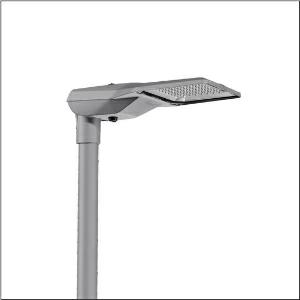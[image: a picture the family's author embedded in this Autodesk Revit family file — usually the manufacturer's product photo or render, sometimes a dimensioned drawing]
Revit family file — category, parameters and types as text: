
# Revit family: streetlight_sl_21_iq_midi___st1_0ab_5xe3m31y08nb_fb51
name_source: partatom
category: Lighting Fixtures
units: mm (PartAtom-declared; Revit-internal decimal feet)

## family parameters
Cut with Voids When Loaded = No
Host = Face
Light Source = No
Part Type = Normal
Room Calculation Point = No
Round Connector Dimension = Use Diameter
Shared = No

## types (1)
- --- (1 x LED, 18970 lm, 136.6 W, 3000K)
    Apparent Load = 137 VA
    CIE Flux Codes = 40 74 97 100 100
    Color Rendering = 70
    Color Temperature = 3000K
    Default Elevation = 1800 mm
    Description = Streetlight SL 21 iQ midi, mast luminaire, primary light control with lens, of PMMA, primary optical cover: cover, of toughened safety glass, transparent, light distribution: ST1.0aB, light emission: direct distribution, primary light characteristic: asymmetric, installation type: post-top, side-entry, LED, High Power LED, rated luminous flux: 18.970lm, luminous efficacy: 139lm/W, light colour: 730, colour temperature: 3000K, control: presetting dimming logarithmic, Street-Remote, Auto-Match, Temp-Guard, Lumen-Switch, Night-Set, Smart-Wire, Light-Fading, Desk-Remote (wireless, voltage-free reading and setting of iQ features in the workshop via application-optimized NFC function/RFID function), optimised constant luminous flux control (CLO 2.0), mains connection: 230..240V, AC, 50/60Hz, start of lifetime: 137W, end of service life: 144W, reduction: 61W, luminaire housing, of diecast aluminium, powder-coated, Siteco® metallic grey (DB 702S), corrosivity category C5 mid according to DIN EN ISO 12944, please order mast flange separately, inclination adjustable: 0°, 5°, 10°, 15°, sealing non-destructively replaceable, multi-level sealing system, length: 644mm, width: 335mm, height: 110mm, mast flange for spigot size: 42mm (side-entry): 5XC10008XM4, 60/48mm (side-entry/post-top): 5XC10108XM2, 76/60mm (side-entry/post-top): 5XC10108XM1, Smart Interface below and above, protection rating (complete): IP66, insulation class (complete): insulation class II (safety insulation), certification: CE, ENEC, ENEC+, VDE, impact resistance: IK09, permissible operating ambient temperature for outdoor applications: -40..+50°C, standard-compliant lighting for roads and squares, packaging unit: 1 piece

Light Distribution: ST1.0aB
    Height = 111 mm
    Lamp = 1 x LED
    Lamp Light Flux = 18970 lm
    Lamp Power = 136.6 W
    Lamp count = 1
    Length = 644 mm
    Luminous efficacy = 139 lm/W
    Manufacturer = Siteco
    ModVariant = No
    Model = 5XE3M31Y08NB
    Number of Poles = 1
    OnlyDefault = Yes
    Power Factor = 1
    Product Name = Streetlight SL 21 iQ midi | ST1.0aB
    Product group = mast luminaire | pylon top
    ProductGroupID = 6100
    Protection Class = Protection class II
    Protection Degree = IP 66
    RLX_Detail_Level = 1
    RLX_Emergency_Light_Flux = 0 lm
    RLX_Emergency_Type = 0
    RLX_Emergency_Type_DB = No
    RlxData = <blob elided: 91005 chars, md5=492decc8>
    Socket = socket
    Standby Power = 0 W
    System Light Flux = 18970 lm
    System Power = 137 W
    Type Comments = factory setting: luminous flux: 100 % | dim-lin: 254 | 733 mA
    Type Image = l_1004304.jpg
    URL = http://relux.com
    VarID = @adj_042141
    Voltage = 0 V
    Weight = 0.00 kg
    Width = 336 mm

## geometry (parser evidence)
native form markers: Blend x4, Sweep x12
no freeform markers — native parametric forms only
